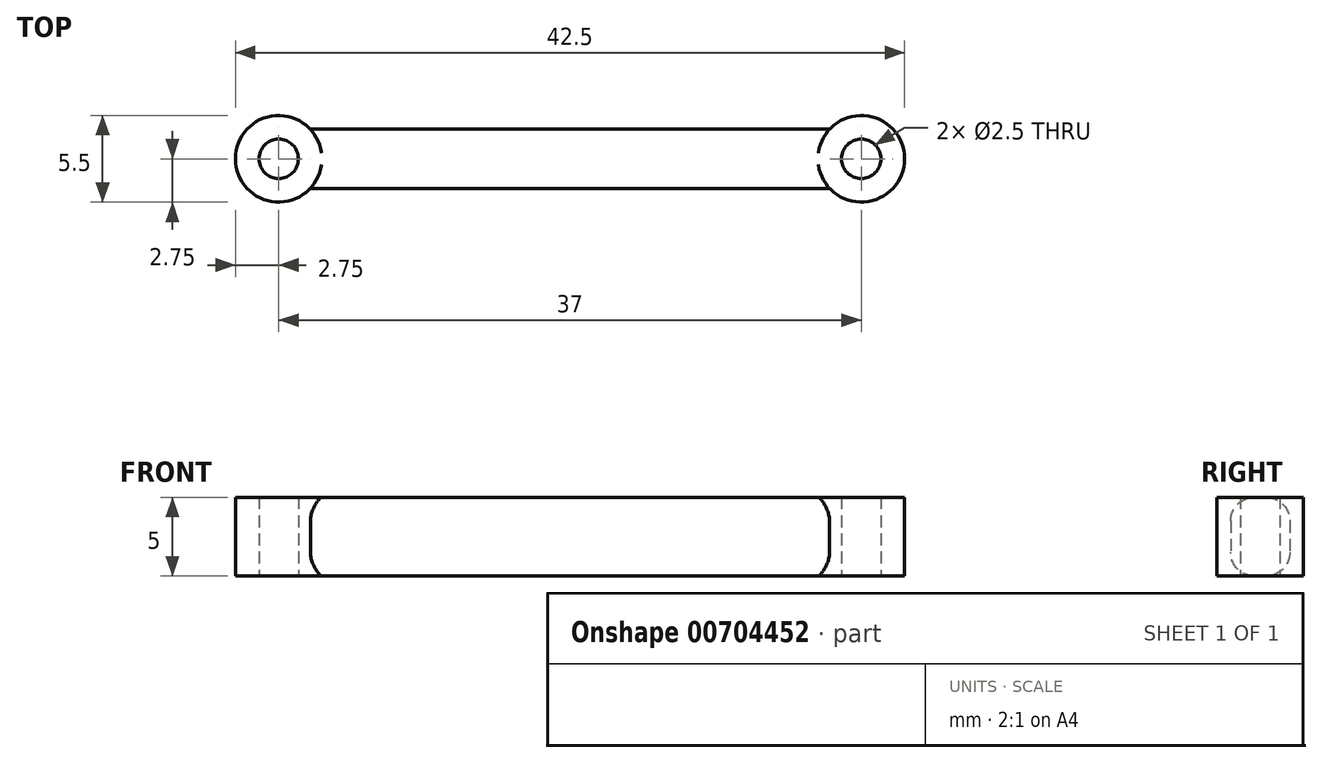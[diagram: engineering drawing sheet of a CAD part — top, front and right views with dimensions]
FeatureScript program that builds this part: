
annotation { "Feature Type Name" : "Feature", "Feature Type Description" : "" }
export const myFeature = defineFeature(function(context is Context, id is Id, definition is map)
    precondition{}
    {
        {
            var Q0;
            Q0=qCreatedBy(makeId("Top.planeOp"),FACE);
            var sketch = newSketch(context, id + "F0", { "sketchPlane" : qUnion([Q0])});
            skCircle(sketch, "E0", {"center": v(0, 0) * mm, "radius": 1.25 * mm});
            skCircle(sketch, "E1", {"center": v(37, 0) * mm, "radius": 1.25 * mm});
            skCircle(sketch, "E2", {"center": v(0, 0) * mm, "radius": 2.75 * mm});
            skCircle(sketch, "E3", {"center": v(37, 0) * mm, "radius": 2.75 * mm});
            skLineSegment(sketch, "E4", {"start": v(2.01, 1.88) * mm, "end": v(34.99, 1.88) * mm});
            skLineSegment(sketch, "E5.MirrorCS", {"start": v(2.01, -1.88) * mm, "end": v(34.99, -1.88) * mm});
            skSolve(sketch);
        }
        {
            var Q0;
            {var subQ0=sQuery(id+"F0.wireOp",EDGE,"E4");Q0=makeQuery(id+"F0.imprint","IMPRINT",FACE,{"disambiguationData":[TD([[makeQuery(id+"F0.imprint","IMPRINT",EDGE,{"derivedFrom":subQ0}),-1.0]])]});}
            var Q1;
            Q1=makeQuery(id+"F0.imprint","IMPRINT",FACE,{"disambiguationData":[TD([[makeQuery(id+"F0.imprint","IMPRINT",EDGE,{"derivedFrom":sQuery(id+"F0.wireOp",EDGE,"E0")}),-1.0]])]});
            var Q2;
            Q2=makeQuery(id+"F0.imprint","IMPRINT",FACE,{"disambiguationData":[TD([[makeQuery(id+"F0.imprint","IMPRINT",EDGE,{"derivedFrom":sQuery(id+"F0.wireOp",EDGE,"E1")}),-1.0]])]});
            extrude(context, id + "F1", {"entities" : qUnion([Q0, Q1, Q2]), "depth" : 5 * mm, "offsetDistance" : 25 * mm, "symmetric" : true});
        }
        {
            var Q0;
            Q0=makeQuery(id+"F1.opExtrude","CAP_EDGE",EDGE,{"disambiguationData":[OSD([sQuery(id+"F0.wireOp",EDGE,"E4")])],"isStart":false});
            var Q1;
            Q1=makeQuery(id+"F1.opExtrude","CAP_EDGE",EDGE,{"disambiguationData":[OSD([sQuery(id+"F0.wireOp",EDGE,"E5.MirrorCS")])],"isStart":false});
            var Q2;
            Q2=makeQuery(id+"F1.opExtrude","CAP_EDGE",EDGE,{"disambiguationData":[OSD([sQuery(id+"F0.wireOp",EDGE,"E5.MirrorCS")])],"isStart":true});
            var Q3;
            Q3=makeQuery(id+"F1.opExtrude","CAP_EDGE",EDGE,{"disambiguationData":[OSD([sQuery(id+"F0.wireOp",EDGE,"E4")])],"isStart":true});
            fillet(context, id + "F2", {"entities" : qUnion([Q0, Q1, Q2, Q3]), "tangentPropagation" : true, "radius" : 1.5 * mm, "defaultsChanged" : false, "vertexSettings" : [], "allowEdgeOverflow" : false});
        }
    });
